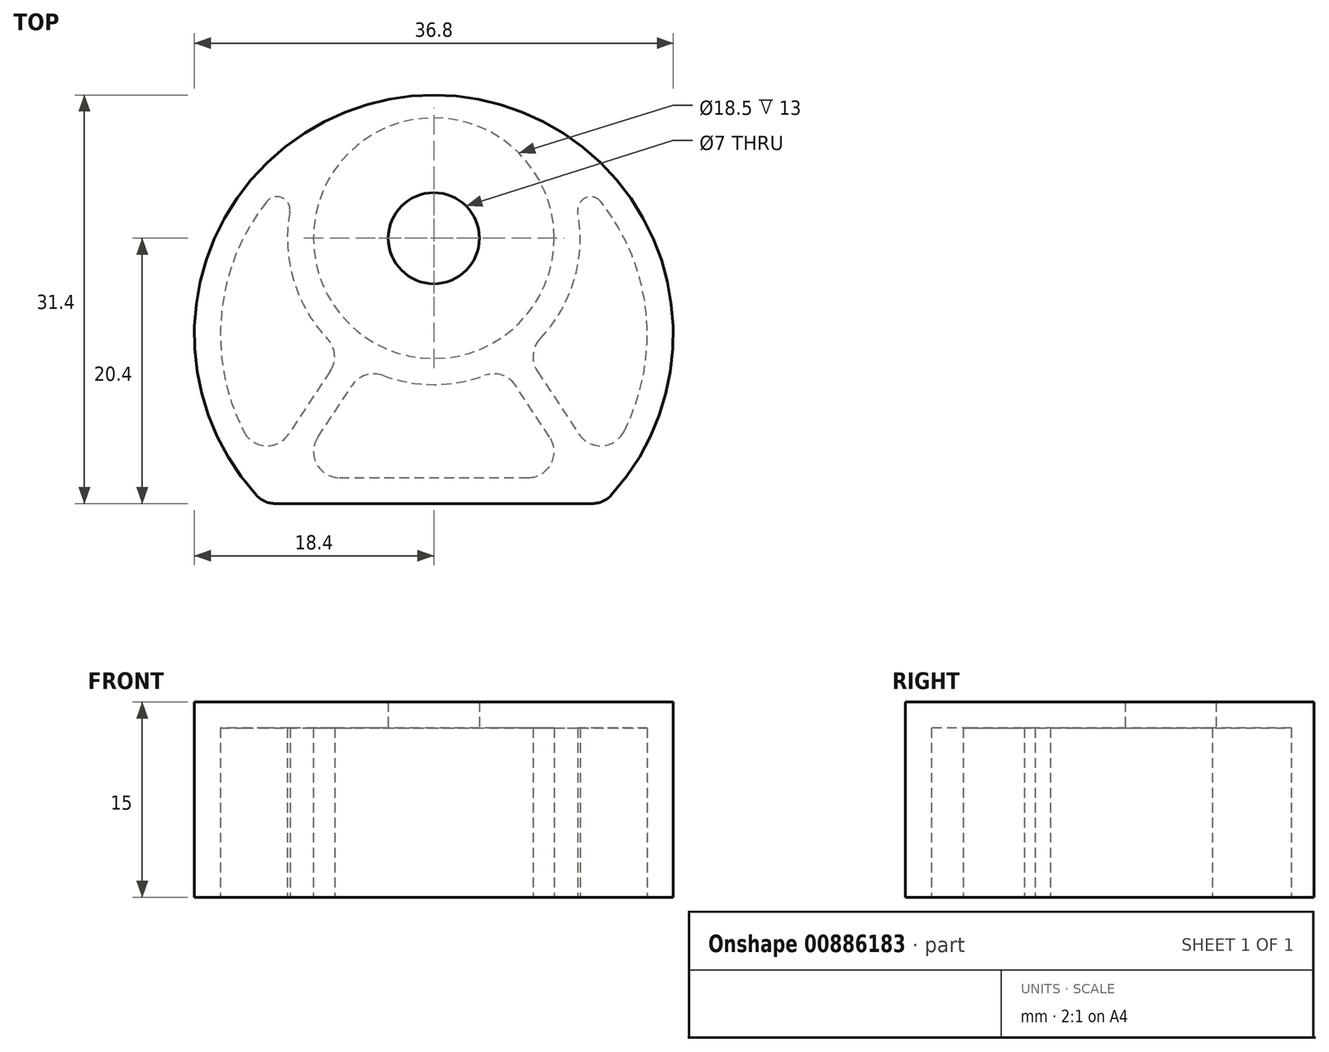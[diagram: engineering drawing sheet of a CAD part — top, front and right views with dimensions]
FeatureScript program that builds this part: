
annotation { "Feature Type Name" : "Feature", "Feature Type Description" : "" }
export const myFeature = defineFeature(function(context is Context, id is Id, definition is map)
    precondition{}
    {
        {
            var Q0;
            Q0=qCreatedBy(makeId("Top.planeOp"),FACE);
            var sketch = newSketch(context, id + "F0", { "sketchPlane" : qUnion([Q0])});
            skArc(sketch, "E0", {"start": v(13.65, -12.34) * mm, "mid": v(0, 18.4) * mm, "end": v(-13.65, -12.34) * mm});
            skArc(sketch, "E1", {"start": v(14.6, -7.47) * mm, "mid": v(16.32, 1.63) * mm, "end": v(12.84, 10.2) * mm});
            skCircle(sketch, "E2", {"center": v(0, 7.4) * mm, "radius": 9.25 * mm});
            skArc(sketch, "E3", {"start": v(-11.07, 9.4) * mm, "mid": v(-10.78, 4.19) * mm, "end": v(-8.17, -0.34) * mm});
            skLineSegment(sketch, "E4", {"start": v(-12.16, -13) * mm, "end": v(12.16, -13) * mm});
            skLineSegment(sketch, "E5", {"start": v(-7.25, -11) * mm, "end": v(7.25, -11) * mm});
            skArc(sketch, "E6.trimOffspring", {"start": v(-12.84, 10.2) * mm, "mid": v(-16.32, 1.63) * mm, "end": v(-14.6, -7.47) * mm});
            skLineSegment(sketch, "E7", {"start": v(-12.16, -11) * mm, "end": v(0, 7.4) * mm, "construction": true});
            skLineSegment(sketch, "E8", {"start": v(12.16, -11) * mm, "end": v(0, 7.4) * mm, "construction": true});
            skLineSegment(sketch, "E9", {"start": v(-8.91, -7.9) * mm, "end": v(-6.28, -3.92) * mm});
            skLineSegment(sketch, "E10", {"start": v(-7.95, -2.81) * mm, "end": v(-11.15, -7.66) * mm});
            skLineSegment(sketch, "E11", {"start": v(8.91, -7.9) * mm, "end": v(6.28, -3.92) * mm});
            skLineSegment(sketch, "E12", {"start": v(7.95, -2.81) * mm, "end": v(11.15, -7.66) * mm});
            skArc(sketch, "E13.trimOffspring", {"start": v(8.17, -0.34) * mm, "mid": v(10.78, 4.19) * mm, "end": v(11.07, 9.4) * mm});
            skArc(sketch, "E14.trimOffspring", {"start": v(-3.92, -3.15) * mm, "mid": v(0, -3.85) * mm, "end": v(3.92, -3.15) * mm});
            skPoint(sketch, "E15.visualSharp", {"position": v(12.84, -10.2) * mm});
            skArc(sketch, "E15.filletArc", {"start": v(11.15, -7.66) * mm, "mid": v(12.93, -8.55) * mm, "end": v(14.6, -7.47) * mm});
            skPoint(sketch, "E16.visualSharp", {"position": v(10.97, -11) * mm});
            skArc(sketch, "E16.filletArc", {"start": v(7.25, -11) * mm, "mid": v(9, -9.95) * mm, "end": v(8.91, -7.9) * mm});
            skPoint(sketch, "E17.visualSharp", {"position": v(13.02, -13) * mm});
            skArc(sketch, "E17.filletArc", {"start": v(12.16, -13) * mm, "mid": v(12.98, -12.83) * mm, "end": v(13.65, -12.34) * mm});
            skPoint(sketch, "E18.visualSharp", {"position": v(-13.02, -13) * mm});
            skArc(sketch, "E18.filletArc", {"start": v(-13.65, -12.34) * mm, "mid": v(-12.98, -12.83) * mm, "end": v(-12.16, -13) * mm});
            skPoint(sketch, "E19.visualSharp", {"position": v(-10.97, -11) * mm});
            skArc(sketch, "E19.filletArc", {"start": v(-8.91, -7.9) * mm, "mid": v(-9, -9.95) * mm, "end": v(-7.25, -11) * mm});
            skPoint(sketch, "E20.visualSharp", {"position": v(-12.84, -10.2) * mm});
            skArc(sketch, "E20.filletArc", {"start": v(-14.6, -7.47) * mm, "mid": v(-12.93, -8.55) * mm, "end": v(-11.15, -7.66) * mm});
            skPoint(sketch, "E21.visualSharp", {"position": v(-5.35, -2.5) * mm});
            skArc(sketch, "E21.filletArc", {"start": v(-3.92, -3.15) * mm, "mid": v(-5.24, -3.12) * mm, "end": v(-6.28, -3.92) * mm});
            skPoint(sketch, "E22.visualSharp", {"position": v(5.35, -2.5) * mm});
            skArc(sketch, "E22.filletArc", {"start": v(6.28, -3.92) * mm, "mid": v(5.24, -3.12) * mm, "end": v(3.92, -3.15) * mm});
            skPoint(sketch, "E23.visualSharp", {"position": v(7.01, -1.4) * mm});
            skArc(sketch, "E23.filletArc", {"start": v(8.17, -0.34) * mm, "mid": v(7.63, -1.54) * mm, "end": v(7.95, -2.81) * mm});
            skPoint(sketch, "E24.visualSharp", {"position": v(-7.01, -1.4) * mm});
            skArc(sketch, "E24.filletArc", {"start": v(-7.95, -2.81) * mm, "mid": v(-7.63, -1.54) * mm, "end": v(-8.17, -0.34) * mm});
            skPoint(sketch, "E25.visualSharp", {"position": v(9.57, 13.32) * mm});
            skArc(sketch, "E25.filletArc", {"start": v(12.84, 10.2) * mm, "mid": v(11.64, 10.5) * mm, "end": v(11.07, 9.4) * mm});
            skPoint(sketch, "E26.visualSharp", {"position": v(-9.57, 13.32) * mm});
            skArc(sketch, "E26.filletArc", {"start": v(-11.07, 9.4) * mm, "mid": v(-11.64, 10.5) * mm, "end": v(-12.84, 10.2) * mm});
            skLineSegment(sketch, "E27", {"start": v(-13.01, 18.4) * mm, "end": v(13.67, 18.4) * mm, "construction": true});
            skSolve(sketch);
        }
        {
            var Q0;
            Q0=makeQuery(id+"F0.imprint","IMPRINT",FACE,{"disambiguationData":[TD([[makeQuery(id+"F0.imprint","IMPRINT",EDGE,{"derivedFrom":sQuery(id+"F0.wireOp",EDGE,"E0")}),1.0]])]});
            extrude(context, id + "F1", {"entities" : qUnion([Q0]), "depth" : 13 * mm, "offsetDistance" : 25 * mm});
        }
        {
            var Q0;
            Q0=makeQuery(id+"F1.opExtrude","CAP_FACE",FACE,{"disambiguationData":[OSD([sQuery(id+"F0.wireOp",EDGE,"E0"),sQuery(id+"F0.wireOp",EDGE,"E1"),sQuery(id+"F0.wireOp",EDGE,"E2"),sQuery(id+"F0.wireOp",EDGE,"E3"),sQuery(id+"F0.wireOp",EDGE,"E4"),sQuery(id+"F0.wireOp",EDGE,"E5"),sQuery(id+"F0.wireOp",EDGE,"E6.trimOffspring"),sQuery(id+"F0.wireOp",EDGE,"E9"),sQuery(id+"F0.wireOp",EDGE,"E10"),sQuery(id+"F0.wireOp",EDGE,"E11"),sQuery(id+"F0.wireOp",EDGE,"E12"),sQuery(id+"F0.wireOp",EDGE,"E13.trimOffspring"),sQuery(id+"F0.wireOp",EDGE,"E14.trimOffspring"),sQuery(id+"F0.wireOp",EDGE,"E15.filletArc"),sQuery(id+"F0.wireOp",EDGE,"E16.filletArc"),sQuery(id+"F0.wireOp",EDGE,"E17.filletArc"),sQuery(id+"F0.wireOp",EDGE,"E18.filletArc"),sQuery(id+"F0.wireOp",EDGE,"E19.filletArc"),sQuery(id+"F0.wireOp",EDGE,"E20.filletArc"),sQuery(id+"F0.wireOp",EDGE,"E21.filletArc"),sQuery(id+"F0.wireOp",EDGE,"E22.filletArc"),sQuery(id+"F0.wireOp",EDGE,"E23.filletArc"),sQuery(id+"F0.wireOp",EDGE,"E24.filletArc"),sQuery(id+"F0.wireOp",EDGE,"E25.filletArc"),sQuery(id+"F0.wireOp",EDGE,"E26.filletArc")])],"isStart":false});
            var sketch = newSketch(context, id + "F2", { "sketchPlane" : qUnion([Q0])});
            skArc(sketch, "E28.0", {"start": v(13.65, -12.34) * mm, "mid": v(0, 18.4) * mm, "end": v(-13.65, -12.34) * mm});
            skArc(sketch, "E28.1", {"start": v(12.16, -13) * mm, "mid": v(12.98, -12.83) * mm, "end": v(13.65, -12.34) * mm});
            skLineSegment(sketch, "E28.2", {"start": v(-12.16, -13) * mm, "end": v(12.16, -13) * mm});
            skArc(sketch, "E28.3", {"start": v(-13.65, -12.34) * mm, "mid": v(-12.98, -12.83) * mm, "end": v(-12.16, -13) * mm});
            skCircle(sketch, "E29", {"center": v(0, 7.4) * mm, "radius": 3.5 * mm});
            skSolve(sketch);
        }
        {
            var Q0;
            Q0 = qSketchRegion(id + "F2", true);
            extrude(context, id + "F3", {"entities" : qUnion([Q0]), "operationType" : NewBodyOperationType.ADD, "depth" : 2 * mm, "offsetDistance" : 25 * mm});
        }
    });
